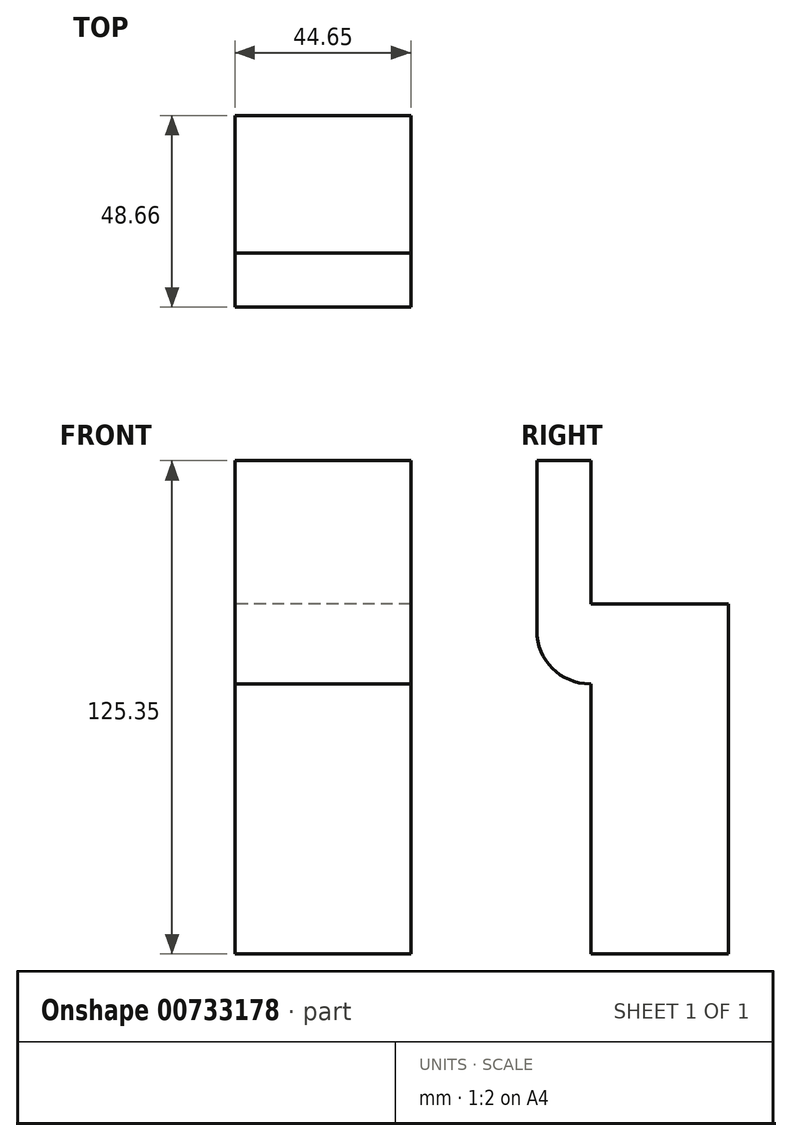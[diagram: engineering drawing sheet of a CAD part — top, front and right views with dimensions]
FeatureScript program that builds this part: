
annotation { "Feature Type Name" : "Feature", "Feature Type Description" : "" }
export const myFeature = defineFeature(function(context is Context, id is Id, definition is map)
    precondition{}
    {
        {
            var Q0;
            Q0=qCreatedBy(makeId("Top.planeOp"),FACE);
            var sketch = newSketch(context, id + "F0", { "sketchPlane" : qUnion([Q0])});
            skLineSegment(sketch, "E0.bottom", {"start": v(55.49, 24.98) * mm, "end": v(10.84, 24.98) * mm});
            skLineSegment(sketch, "E0.top", {"start": v(55.49, -9.96) * mm, "end": v(10.84, -9.96) * mm});
            skLineSegment(sketch, "E0.left", {"start": v(55.49, 24.98) * mm, "end": v(55.49, -9.96) * mm});
            skLineSegment(sketch, "E0.right", {"start": v(10.84, 24.98) * mm, "end": v(10.84, -9.96) * mm});
            skSolve(sketch);
        }
        {
            var Q0;
            Q0=makeQuery(id+"F0.imprint","IMPRINT",FACE,{"disambiguationData":[TD([[makeQuery(id+"F0.imprint","IMPRINT",EDGE,{"derivedFrom":sQuery(id+"F0.wireOp",EDGE,"E0.bottom")}),1.0]])]});
            extrude(context, id + "F1", {"entities" : qUnion([Q0]), "depth" : 88.9 * mm, "offsetDistance" : 25.4 * mm});
        }
        {
            var Q0;
            Q0=makeQuery(id+"F1.opExtrude","SWEPT_FACE",FACE,{"disambiguationData":[OSD([sQuery(id+"F0.wireOp",EDGE,"E0.top")])]});
            var sketch = newSketch(context, id + "F2", { "sketchPlane" : qUnion([Q0])});
            skLineSegment(sketch, "E1.bottom", {"start": v(10.84, 68.64) * mm, "end": v(55.49, 68.64) * mm});
            skLineSegment(sketch, "E1.top", {"start": v(10.84, 125.35) * mm, "end": v(55.49, 125.35) * mm});
            skLineSegment(sketch, "E1.left", {"start": v(10.84, 68.64) * mm, "end": v(10.84, 125.35) * mm});
            skLineSegment(sketch, "E1.right", {"start": v(55.49, 68.64) * mm, "end": v(55.49, 125.35) * mm});
            skSolve(sketch);
        }
        {
            var Q0;
            Q0 = qSketchRegion(id + "F2", true);
            extrude(context, id + "F3", {"entities" : qUnion([Q0]), "operationType" : NewBodyOperationType.ADD, "depth" : 13.72 * mm, "offsetDistance" : 25.4 * mm});
        }
        {
            var Q0;
            Q0=makeQuery(id+"F3.opExtrude","CAP_EDGE",EDGE,{"disambiguationData":[OSD([sQuery(id+"F2.wireOp",EDGE,"E1.bottom")])],"isStart":false});
            var Q1;
            Q1=makeQuery(id+"F5rJ6YXqTXEWmuJ_1.opExtrude","CAP_EDGE",EDGE,{"disambiguationData":[OSD([sQuery(id+"FyDMcZfRPtr2x6O_1.wireOp",EDGE,"h9OInBf8-0uGl-oqhn-5EPh-fMWykFzlCXJK.bottom")])],"isStart":false});
            fillet(context, id + "F4", {"entities" : qUnion([Q0, Q1]), "radius" : 13.5 * mm, "tangentPropagation" : true, "allowEdgeOverflow" : false});
        }
    });
